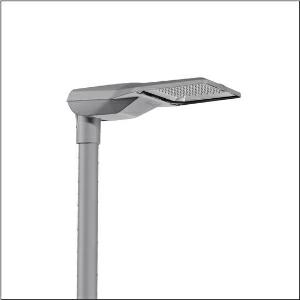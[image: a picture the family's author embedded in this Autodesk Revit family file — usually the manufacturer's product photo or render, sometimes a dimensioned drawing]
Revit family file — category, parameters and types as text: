
# Revit family: streetlight_sl_21_iq_midi___pl52_5xe3h41d08mb_c975
name_source: partatom
category: Lighting Fixtures
units: mm (PartAtom-declared; Revit-internal decimal feet)

## family parameters
Cut with Voids When Loaded = No
Host = Face
Light Source = No
Part Type = Normal
Room Calculation Point = No
Round Connector Dimension = Use Diameter
Shared = No

## types (1)
- --- (1 x LED, 20000 lm, 146.7 W, 4000K)
    Apparent Load = 147 VA
    CIE Flux Codes = 27 59 98 100 100
    Color Rendering = 70
    Color Temperature = 4000K
    Default Elevation = 1800 mm
    Description = Streetlight SL 21 iQ midi, mast luminaire, primary light control with lens, of PMMA, primary optical cover: cover, of toughened safety glass, transparent, light distribution: PL52, light emission: direct distribution, primary light characteristic: asymmetric, installation type: post-top, side-entry, LED, High Power LED, rated luminous flux: 20.000lm, luminous efficacy: 136lm/W, light colour: 740, colour temperature: 4000K, control: Auto-Match, Temp-Guard, Lumen-Switch, Night-Set, Smart-Wire, Light-Fading, Desk-Remote (wireless, voltage-free reading and setting of iQ features in the workshop via application-optimized NFC function/RFID function), optimised constant luminous flux control (CLO 2.0), presetting dimming linear, mains connection: 230..240V, AC, 50/60Hz, start of lifetime: 147W, end of service life: 161W, reduction: 62W, luminaire housing, of diecast aluminium, powder-coated, Siteco® metallic grey (DB 702S), corrosivity category C5 mid according to DIN EN ISO 12944, please order mast flange separately, inclination adjustable: 0°, 5°, 10°, 15°, sealing non-destructively replaceable, multi-level sealing system, length: 644mm, width: 335mm, height: 110mm, mast flange for spigot size: 42mm (side-entry): 5XC10008XM4, 60/48mm (side-entry/post-top): 5XC10108XM2, 76/60mm (side-entry/post-top): 5XC10108XM1, protection rating (complete): IP66, insulation class (complete): insulation class II (safety insulation), certification: CE, ENEC, ENEC+, VDE, impact resistance: IK09, permissible operating ambient temperature for outdoor applications: -40..+50°C, standard-compliant lighting for roads and squares, packaging unit: 1 piece

Light Distribution: PL52
    Height = 111 mm
    Lamp = 1 x LED
    Lamp Light Flux = 20000 lm
    Lamp Power = 146.7 W
    Lamp count = 1
    Length = 644 mm
    Luminous efficacy = 136 lm/W
    Manufacturer = Siteco
    ModVariant = No
    Model = 5XE3H41D08MB
    Number of Poles = 1
    OnlyDefault = Yes
    Power Factor = 1
    Product Name = Streetlight SL 21 iQ midi | PL52
    Product group = mast luminaire | pylon top
    ProductGroupID = 6100
    Protection Class = Protection class II
    Protection Degree = IP 66
    RLX_Detail_Level = 1
    RLX_Emergency_Light_Flux = 0 lm
    RLX_Emergency_Type = 0
    RLX_Emergency_Type_DB = No
    RlxData = <blob elided: 100645 chars, md5=f8e4af79>
    Socket = socket
    Standby Power = 0 W
    System Light Flux = 20000 lm
    System Power = 147 W
    Type Comments = factory setting: luminous flux: 100 % | dim-lin: 254 | 753 mA
    Type Image = l_1004298.jpg
    URL = http://relux.com
    VarID = @adj_124885
    Voltage = 0 V
    Weight = 0.00 kg
    Width = 336 mm

## geometry (parser evidence)
native form markers: Blend x4, Sweep x11
no freeform markers — native parametric forms only
